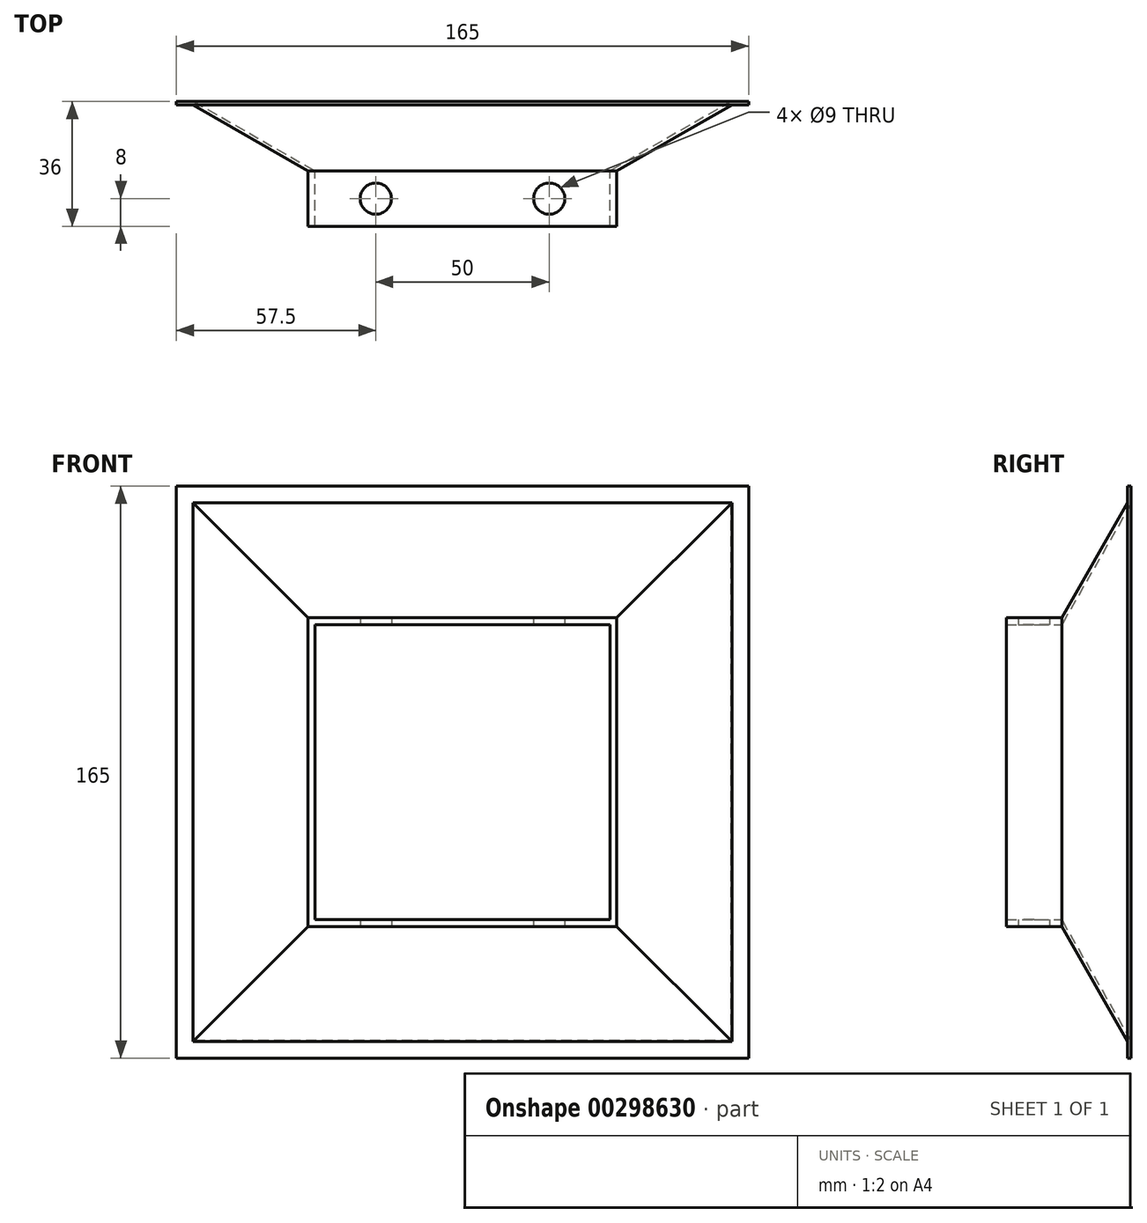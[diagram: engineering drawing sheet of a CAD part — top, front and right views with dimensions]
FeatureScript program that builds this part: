
annotation { "Feature Type Name" : "Feature", "Feature Type Description" : "" }
export const myFeature = defineFeature(function(context is Context, id is Id, definition is map)
    precondition{}
    {
        {
            var Q0;
            Q0=qCreatedBy(makeId("Front.planeOp"),FACE);
            var sketch = newSketch(context, id + "F0", { "sketchPlane" : qUnion([Q0])});
            skLineSegment(sketch, "E0.bottom", {"start": v(-82.5, 82.5) * mm, "end": v(82.5, 82.5) * mm});
            skLineSegment(sketch, "E0.top", {"start": v(-82.5, -82.5) * mm, "end": v(82.5, -82.5) * mm});
            skLineSegment(sketch, "E0.left", {"start": v(-82.5, 82.5) * mm, "end": v(-82.5, -82.5) * mm});
            skLineSegment(sketch, "E0.right", {"start": v(82.5, 82.5) * mm, "end": v(82.5, -82.5) * mm});
            skLineSegment(sketch, "E1.bottom", {"start": v(77.5, -77.5) * mm, "end": v(-77.5, -77.5) * mm});
            skLineSegment(sketch, "E1.top", {"start": v(77.5, 77.5) * mm, "end": v(-77.5, 77.5) * mm});
            skLineSegment(sketch, "E1.left", {"start": v(77.5, -77.5) * mm, "end": v(77.5, 77.5) * mm});
            skLineSegment(sketch, "E1.right", {"start": v(-77.5, -77.5) * mm, "end": v(-77.5, 77.5) * mm});
            skPoint(sketch, "E1.middle", {"position": v(0, 0) * mm});
            skSolve(sketch);
        }
        {
            var Q0;
            Q0=makeQuery(id+"F0.imprint","IMPRINT",FACE,{"disambiguationData":[TD([[makeQuery(id+"F0.imprint","IMPRINT",EDGE,{"derivedFrom":sQuery(id+"F0.wireOp",EDGE,"E0.bottom")}),-1.0]])]});
            cPlane(context, id + "F1", {"entities" : qUnion([Q0]), "cplaneType" : CPlaneType.OFFSET, "offset" : 20 * mm, "width" : 150 * mm, "height" : 150 * mm});
        }
        {
            var Q0;
            Q0=qCreatedBy(id+"F1.planeOp",FACE);
            var sketch = newSketch(context, id + "F2", { "sketchPlane" : qUnion([Q0])});
            skLineSegment(sketch, "E2.bottom", {"start": v(42.5, -42.5) * mm, "end": v(-42.5, -42.5) * mm});
            skLineSegment(sketch, "E2.top", {"start": v(42.5, 42.5) * mm, "end": v(-42.5, 42.5) * mm});
            skLineSegment(sketch, "E2.left", {"start": v(42.5, -42.5) * mm, "end": v(42.5, 42.5) * mm});
            skLineSegment(sketch, "E2.right", {"start": v(-42.5, -42.5) * mm, "end": v(-42.5, 42.5) * mm});
            skPoint(sketch, "E2.middle", {"position": v(0, 0) * mm});
            skSolve(sketch);
        }
        {
            var Q0;
            Q0=makeQuery(id+"F0.imprint","IMPRINT",FACE,{"disambiguationData":[TD([[makeQuery(id+"F0.imprint","IMPRINT",EDGE,{"derivedFrom":sQuery(id+"F0.wireOp",EDGE,"E1.bottom")}),-1.0]])]});
            var Q1;
            Q1=makeQuery(id+"F2.imprint","IMPRINT",FACE,{"disambiguationData":[TD([[makeQuery(id+"F2.imprint","IMPRINT",EDGE,{"derivedFrom":sQuery(id+"F2.wireOp",EDGE,"E2.bottom")}),-1.0]])]});
            loft(context, id + "F3", {"sheetProfilesArray" : [{ "sheetProfileEntities" : qUnion([Q0]) }, { "sheetProfileEntities" : qUnion([Q1]) }]});
        }
        {
            var Q0;
            Q0=makeQuery(id+"F3.opLoft","CAP_FACE",FACE,{"disambiguationData":[OSD([makeQuery(id+"F2.imprint","IMPRINT",FACE,{"disambiguationData":[TD([[makeQuery(id+"F2.imprint","IMPRINT",EDGE,{"derivedFrom":sQuery(id+"F2.wireOp",EDGE,"E2.bottom")}),-1.0]])]})])],"isStart":true});
            var Q1;
            Q1=makeQuery(id+"F3.opLoft","CAP_FACE",FACE,{"disambiguationData":[OSD([makeQuery(id+"F0.imprint","IMPRINT",FACE,{"disambiguationData":[TD([[makeQuery(id+"F0.imprint","IMPRINT",EDGE,{"derivedFrom":sQuery(id+"F0.wireOp",EDGE,"E1.bottom")}),-1.0]])]})])],"isStart":true});
            shell(context, id + "F4", {"entities" : qUnion([Q0, Q1]), "thickness" : 1 * mm, "oppositeDirection" : true});
        }
        {
            var Q0;
            Q0=makeQuery(id+"F0.imprint","IMPRINT",FACE,{"disambiguationData":[TD([[makeQuery(id+"F0.imprint","IMPRINT",EDGE,{"derivedFrom":sQuery(id+"F0.wireOp",EDGE,"E0.bottom")}),-1.0]])]});
            extrude(context, id + "F5", {"entities" : qUnion([Q0]), "operationType" : NewBodyOperationType.ADD, "depth" : 1 * mm});
        }
        {
            var Q0;
            Q0=makeQuery(id+"F3.opLoft","CAP_FACE",FACE,{"disambiguationData":[OSD([makeQuery(id+"F2.imprint","IMPRINT",FACE,{"disambiguationData":[TD([[makeQuery(id+"F2.imprint","IMPRINT",EDGE,{"derivedFrom":sQuery(id+"F2.wireOp",EDGE,"E2.bottom")}),-1.0]])]})])],"isStart":true});
            var sketch = newSketch(context, id + "F6", { "sketchPlane" : qUnion([Q0])});
            skLineSegment(sketch, "E3.0", {"start": v(-42.5, -42.5) * mm, "end": v(42.5, -42.5) * mm});
            skLineSegment(sketch, "E4.0", {"start": v(42.5, -42.5) * mm, "end": v(42.5, 42.5) * mm});
            skLineSegment(sketch, "E5.0", {"start": v(44.52, -44.52) * mm, "end": v(44.52, 44.52) * mm});
            skLineSegment(sketch, "E6.0", {"start": v(44.52, 44.52) * mm, "end": v(-44.52, 44.52) * mm});
            skLineSegment(sketch, "E7.0", {"start": v(42.5, 42.5) * mm, "end": v(-42.5, 42.5) * mm});
            skLineSegment(sketch, "E8.0", {"start": v(-44.52, 44.52) * mm, "end": v(-44.52, -44.52) * mm});
            skLineSegment(sketch, "E9.0", {"start": v(-42.5, 42.5) * mm, "end": v(-42.5, -42.5) * mm});
            skLineSegment(sketch, "E10.0", {"start": v(-44.52, -44.52) * mm, "end": v(44.52, -44.52) * mm});
            skSolve(sketch);
        }
        {
            var Q0;
            Q0=qSketchRegion(id+"F6",true);
            extrude(context, id + "F7", {"entities" : qUnion([Q0]), "operationType" : NewBodyOperationType.ADD, "depth" : 16 * mm});
        }
        {
            var Q0;
            Q0=makeQuery(id+"F7.opExtrude","SWEPT_FACE",FACE,{"disambiguationData":[OSD([sQuery(id+"F6.wireOp",EDGE,"E6.0")])]});
            var sketch = newSketch(context, id + "F8", { "sketchPlane" : qUnion([Q0])});
            skLineSegment(sketch, "E11", {"start": v(44.52, -20) * mm, "end": v(34.52, -20) * mm});
            skLineSegment(sketch, "E12", {"start": v(34.52, -20) * mm, "end": v(27.44, -27.07) * mm});
            skArc(sketch, "E13", {"start": v(21.13, -36) * mm, "mid": v(26.6, -33.17) * mm, "end": v(27.44, -27.07) * mm});
            skLineSegment(sketch, "E14", {"start": v(44.52, -20) * mm, "end": v(44.52, -36) * mm});
            skLineSegment(sketch, "E15", {"start": v(21.13, -36) * mm, "end": v(44.52, -36) * mm});
            skLineSegment(sketch, "E16", {"start": v(-44.52, -20) * mm, "end": v(-34.52, -20) * mm});
            skLineSegment(sketch, "E17", {"start": v(-34.52, -20) * mm, "end": v(-27.44, -27.07) * mm});
            skArc(sketch, "E18", {"start": v(-27.44, -27.07) * mm, "mid": v(-26.6, -33.17) * mm, "end": v(-21.13, -36) * mm});
            skLineSegment(sketch, "E19", {"start": v(-21.13, -36) * mm, "end": v(-44.52, -36) * mm});
            skLineSegment(sketch, "E20", {"start": v(-44.52, -36) * mm, "end": v(-44.52, -20) * mm});
            skSolve(sketch);
        }
        {
            var Q0;
            Q0=makeQuery(id+"F7.opExtrude","SWEPT_FACE",FACE,{"disambiguationData":[OSD([sQuery(id+"F6.wireOp",EDGE,"E10.0")])]});
            var sketch = newSketch(context, id + "F9", { "sketchPlane" : qUnion([Q0])});
            skLineSegment(sketch, "E21", {"start": v(-65.03, 28) * mm, "end": v(85.35, 28) * mm, "construction": true});
            skCircle(sketch, "E22", {"center": v(-25, 28) * mm, "radius": 4.5 * mm});
            skCircle(sketch, "E23", {"center": v(25, 28) * mm, "radius": 4.5 * mm});
            skSolve(sketch);
        }
        {
            var Q0;
            Q0 = qSketchRegion(id + "F9", true);
            extrude(context, id + "F10", {"entities" : qUnion([Q0]), "operationType" : NewBodyOperationType.REMOVE, "oppositeDirection" : true, "depth" : 108 * mm});
        }
    });
